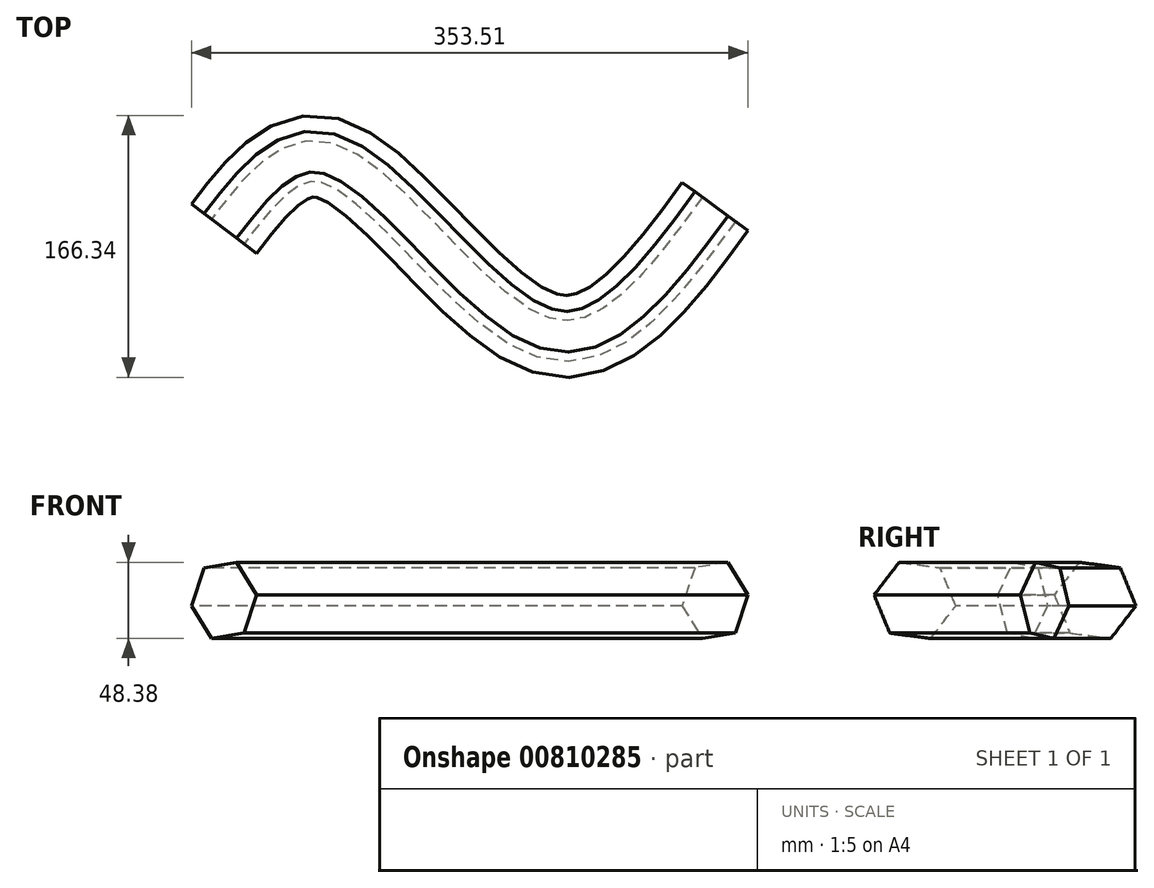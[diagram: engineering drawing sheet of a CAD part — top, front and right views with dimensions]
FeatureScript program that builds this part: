
annotation { "Feature Type Name" : "Feature", "Feature Type Description" : "" }
export const myFeature = defineFeature(function(context is Context, id is Id, definition is map)
    precondition{}
    {
        {
            var Q0;
            Q0=qCreatedBy(makeId("Top.planeOp"),FACE);
            var sketch = newSketch(context, id + "F0", { "sketchPlane" : qUnion([Q0])});
            skFitSpline(sketch, "E0", {"points": [v(-195.05, 15.58) * mm, v(-128.79, 59.9) * mm, v(9.87, -51.56) * mm, v(116.94, 29.62) * mm], "startDerivative": vector(227.03, 296.68) * mm, "endDerivative": vector(295.2, 402.69) * mm});
            skSolve(sketch);
        }
        {
            var Q0;
            Q0=sQuery(id+"F0.wireOp",VERTEX,"E0.end");
            var Q1;
            Q1=sQuery(id+"F0.wireOp",EDGE,"E0");
            cPlane(context, id + "F1", {"entities" : qUnion([Q0, Q1]), "cplaneType" : CPlaneType.CURVE_POINT, "offset" : 25 * mm, "width" : 150 * mm, "height" : 150 * mm});
        }
        {
            var Q0;
            Q0=qCreatedBy(id+"F1.planeOp",FACE);
            var sketch = newSketch(context, id + "F2", { "sketchPlane" : qUnion([Q0])});
            skCircle(sketch, "E1.cCircle", {"center": v(-76.19, 0) * mm, "radius": 22.67 * mm, "construction": true});
            skLineSegment(sketch, "E1.0", {"start": v(-102.14, 3.44) * mm, "end": v(-86.18, 24.2) * mm});
            skLineSegment(sketch, "E1.1", {"start": v(-86.18, 24.2) * mm, "end": v(-60.23, 20.75) * mm});
            skLineSegment(sketch, "E1.2", {"start": v(-60.23, 20.75) * mm, "end": v(-50.24, -3.44) * mm});
            skLineSegment(sketch, "E1.3", {"start": v(-50.24, -3.44) * mm, "end": v(-66.2, -24.2) * mm});
            skLineSegment(sketch, "E1.4", {"start": v(-66.2, -24.2) * mm, "end": v(-92.15, -20.75) * mm});
            skLineSegment(sketch, "E1.5", {"start": v(-92.15, -20.75) * mm, "end": v(-102.14, 3.44) * mm});
            skPoint(sketch, "E1.0.midPoint", {"position": v(-94.16, 13.82) * mm});
            skSolve(sketch);
        }
        {
            var Q0;
            Q0=makeQuery(id+"F2.imprint","IMPRINT",FACE,{"disambiguationData":[TD([[makeQuery(id+"F2.imprint","IMPRINT",EDGE,{"derivedFrom":sQuery(id+"F2.wireOp",EDGE,"E1.0")}),-1.0]])]});
            var Q1;
            Q1=sQuery(id+"F0.wireOp",EDGE,"E0");
            sweep(context, id + "F3", {"profiles" : qUnion([Q0]), "path" : qUnion([Q1])});
        }
    });
